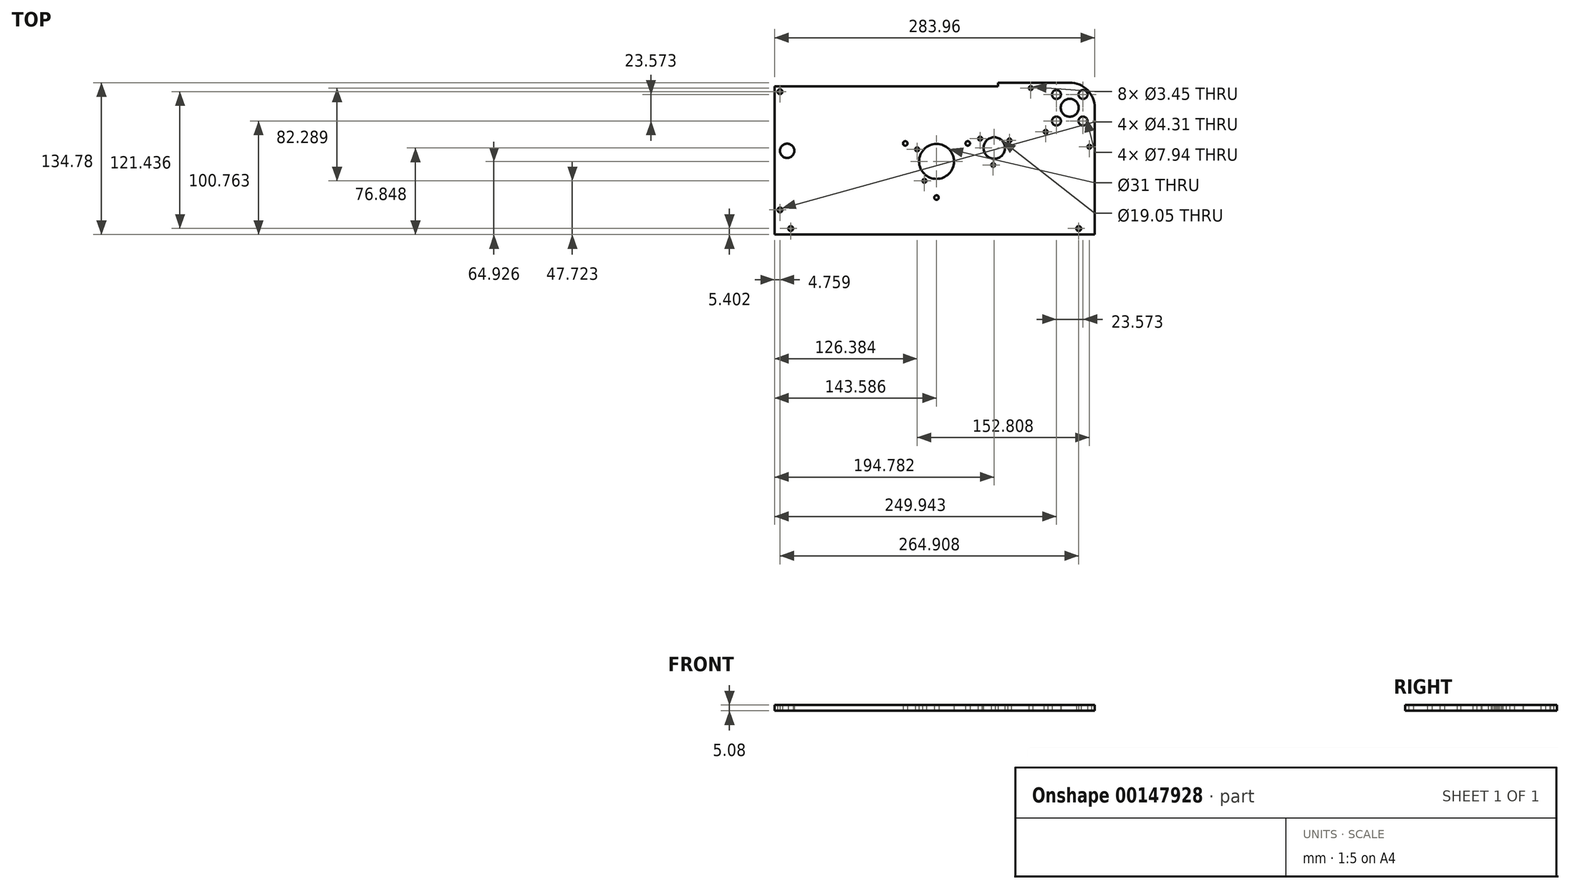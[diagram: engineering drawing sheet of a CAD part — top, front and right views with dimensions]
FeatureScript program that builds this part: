
annotation { "Feature Type Name" : "Feature", "Feature Type Description" : "" }
export const myFeature = defineFeature(function(context is Context, id is Id, definition is map)
    precondition{}
    {
        {
            var Q0;
            Q0=qCreatedBy(makeId("Top.planeOp"),FACE);
            var sketch = newSketch(context, id + "F0", { "sketchPlane" : qUnion([Q0])});
            skCircle(sketch, "E0", {"center": v(0, 0) * mm, "radius": 7.94 * mm});
            skLineSegment(sketch, "E1.bottom", {"start": v(-63.67, 22.23) * mm, "end": v(0, 22.23) * mm});
            skLineSegment(sketch, "E1.top", {"start": v(-261.73, -112.55) * mm, "end": v(22.22, -112.55) * mm});
            skLineSegment(sketch, "E1.left", {"start": v(-261.73, 19.05) * mm, "end": v(-261.73, -112.55) * mm});
            skArc(sketch, "E2", {"start": v(22.23, 0) * mm, "mid": v(15.72, 15.72) * mm, "end": v(0, 22.23) * mm});
            skLineSegment(sketch, "E3", {"start": v(22.23, -112.55) * mm, "end": v(22.23, 0) * mm});
            skLineSegment(sketch, "E4", {"start": v(22.22, -107.15) * mm, "end": v(7.94, -107.15) * mm, "construction": true});
            skCircle(sketch, "E5", {"center": v(7.94, -107.15) * mm, "radius": 2.15 * mm});
            skLineSegment(sketch, "E6", {"start": v(-261.73, -107.15) * mm, "end": v(-247.45, -107.15) * mm, "construction": true});
            skCircle(sketch, "E7", {"center": v(-247.45, -107.15) * mm, "radius": 2.15 * mm});
            skLineSegment(sketch, "E8", {"start": v(-256.97, 19.05) * mm, "end": v(-256.97, 14.29) * mm, "construction": true});
            skLineSegment(sketch, "E9", {"start": v(-256.97, 14.29) * mm, "end": v(-261.73, 14.29) * mm, "construction": true});
            skLineSegment(sketch, "E10", {"start": v(-256.97, 14.29) * mm, "end": v(-256.97, -90.64) * mm, "construction": true});
            skLineSegment(sketch, "E11", {"start": v(-256.97, -90.64) * mm, "end": v(-256.97, -107.15) * mm, "construction": true});
            skCircle(sketch, "E12", {"center": v(-256.97, -90.64) * mm, "radius": 2.15 * mm});
            skCircle(sketch, "E13", {"center": v(-256.97, 14.29) * mm, "radius": 2.15 * mm});
            skCircle(sketch, "E14", {"center": v(-118.14, -47.62) * mm, "radius": 15.5 * mm});
            skCircle(sketch, "E15.cCircle", {"center": v(-118.14, -47.62) * mm, "radius": 16 * mm, "construction": true});
            skLineSegment(sketch, "E15.0", {"start": v(-145.86, -31.62) * mm, "end": v(-90.43, -31.62) * mm, "construction": true});
            skLineSegment(sketch, "E15.1", {"start": v(-90.43, -31.62) * mm, "end": v(-118.14, -79.62) * mm, "construction": true});
            skLineSegment(sketch, "E15.2", {"start": v(-118.14, -79.62) * mm, "end": v(-145.86, -31.62) * mm, "construction": true});
            skPoint(sketch, "E15.0.midPoint", {"position": v(-118.14, -31.62) * mm});
            skLineSegment(sketch, "E16", {"start": v(-118.14, -47.62) * mm, "end": v(-118.14, -79.62) * mm, "construction": true});
            skCircle(sketch, "E17", {"center": v(-145.86, -31.62) * mm, "radius": 2 * mm});
            skCircle(sketch, "E18", {"center": v(-90.43, -31.62) * mm, "radius": 2 * mm});
            skCircle(sketch, "E19", {"center": v(-118.14, -79.62) * mm, "radius": 2 * mm});
            skLineSegment(sketch, "E20", {"start": v(-118.14, -47.62) * mm, "end": v(-66.95, -35.7) * mm, "construction": true});
            skCircle(sketch, "E21", {"center": v(-66.95, -35.7) * mm, "radius": 9.53 * mm});
            skCircle(sketch, "E22", {"center": v(-66.95, -35.7) * mm, "radius": 11.11 * mm, "construction": true});
            skCircle(sketch, "E23", {"center": v(-53.44, -29) * mm, "radius": 3.97 * mm, "construction": true});
            skLineSegment(sketch, "E24", {"start": v(-118.14, -79.62) * mm, "end": v(-118.14, -112.55) * mm, "construction": true});
            skCircle(sketch, "E25", {"center": v(-118.14, -47.62) * mm, "radius": 37.5 * mm, "construction": true});
            skLineSegment(sketch, "E26", {"start": v(-66.95, -35.7) * mm, "end": v(0, 0) * mm, "construction": true});
            skLineSegment(sketch, "E27", {"start": v(-118.14, -47.62) * mm, "end": v(-132.1, -50.87) * mm, "construction": true});
            skLineSegment(sketch, "E28", {"start": v(-135.35, -36.92) * mm, "end": v(-128.85, -64.83) * mm, "construction": true});
            skCircle(sketch, "E29", {"center": v(-135.35, -36.92) * mm, "radius": 4.76 * mm, "construction": true});
            skCircle(sketch, "E30", {"center": v(-135.35, -36.92) * mm, "radius": 1.73 * mm});
            skCircle(sketch, "E31", {"center": v(-128.85, -64.83) * mm, "radius": 1.73 * mm});
            skLineSegment(sketch, "E32", {"start": v(-135.35, -36.92) * mm, "end": v(-118.14, -47.62) * mm, "construction": true});
            skLineSegment(sketch, "E33", {"start": v(0, 0) * mm, "end": v(17.46, -34.55) * mm, "construction": true});
            skLineSegment(sketch, "E34", {"start": v(0, 0) * mm, "end": v(-21.33, -21.33) * mm, "construction": true});
            skLineSegment(sketch, "E35", {"start": v(0, 0) * mm, "end": v(-34.55, 17.46) * mm, "construction": true});
            skCircle(sketch, "E36", {"center": v(-34.55, 17.46) * mm, "radius": 4.76 * mm, "construction": true});
            skCircle(sketch, "E37", {"center": v(-34.55, 17.46) * mm, "radius": 1.73 * mm});
            skCircle(sketch, "E38", {"center": v(-21.33, -21.33) * mm, "radius": 1.73 * mm});
            skCircle(sketch, "E39", {"center": v(17.46, -34.55) * mm, "radius": 1.73 * mm});
            skLineSegment(sketch, "E40", {"start": v(-34.55, 17.46) * mm, "end": v(-21.33, -21.33) * mm, "construction": true});
            skLineSegment(sketch, "E41", {"start": v(17.46, -34.55) * mm, "end": v(-21.33, -21.33) * mm, "construction": true});
            skLineSegment(sketch, "E42", {"start": v(7.94, -107.15) * mm, "end": v(7.94, -112.55) * mm, "construction": true});
            skCircle(sketch, "E43", {"center": v(-90.43, -31.62) * mm, "radius": 6.48 * mm, "construction": true});
            skCircle(sketch, "E44", {"center": v(-66.95, -35.7) * mm, "radius": 17.36 * mm, "construction": true});
            skCircle(sketch, "E45", {"center": v(11.79, 11.79) * mm, "radius": 5.56 * mm, "construction": true});
            skCircle(sketch, "E46", {"center": v(11.79, 11.79) * mm, "radius": 3.97 * mm});
            skCircle(sketch, "E47", {"center": v(11.79, -11.79) * mm, "radius": 3.97 * mm});
            skCircle(sketch, "E48", {"center": v(-11.79, 11.79) * mm, "radius": 3.97 * mm});
            skLineSegment(sketch, "E49.bottom", {"start": v(11.79, 11.79) * mm, "end": v(-11.79, 11.79) * mm, "construction": true});
            skLineSegment(sketch, "E49.top", {"start": v(11.79, -11.79) * mm, "end": v(-11.79, -11.79) * mm, "construction": true});
            skLineSegment(sketch, "E49.left", {"start": v(11.79, 11.79) * mm, "end": v(11.79, -11.79) * mm, "construction": true});
            skLineSegment(sketch, "E49.right", {"start": v(-11.79, 11.79) * mm, "end": v(-11.79, -11.79) * mm, "construction": true});
            skCircle(sketch, "E50", {"center": v(-11.79, -11.79) * mm, "radius": 3.97 * mm});
            skCircle(sketch, "E51.cCircle", {"center": v(-66.95, -35.7) * mm, "radius": 7.54 * mm, "construction": true});
            skLineSegment(sketch, "E51.0", {"start": v(-67.9, -50.75) * mm, "end": v(-79.5, -27.35) * mm, "construction": true});
            skLineSegment(sketch, "E51.1", {"start": v(-79.5, -27.35) * mm, "end": v(-53.44, -29) * mm, "construction": true});
            skLineSegment(sketch, "E51.2", {"start": v(-53.44, -29) * mm, "end": v(-67.9, -50.75) * mm, "construction": true});
            skCircle(sketch, "E52", {"center": v(-79.5, -27.35) * mm, "radius": 1.73 * mm});
            skCircle(sketch, "E53", {"center": v(-67.9, -50.75) * mm, "radius": 1.73 * mm});
            skCircle(sketch, "E54", {"center": v(-53.44, -29) * mm, "radius": 1.73 * mm});
            skCircle(sketch, "E55", {"center": v(-90.43, -31.62) * mm, "radius": 6.17 * mm, "construction": true});
            skCircle(sketch, "E56", {"center": v(-79.5, -27.35) * mm, "radius": 5.56 * mm, "construction": true});
            skLineSegment(sketch, "E57.top", {"start": v(-63.67, 19.05) * mm, "end": v(-261.73, 19.05) * mm});
            skLineSegment(sketch, "E57.left", {"start": v(-63.67, 22.23) * mm, "end": v(-63.67, 19.05) * mm});
            skCircle(sketch, "E58", {"center": v(0, 0) * mm, "radius": 63.67 * mm, "construction": true});
            skLineSegment(sketch, "E59", {"start": v(-63.67, 19.05) * mm, "end": v(-63.67, -8.33) * mm, "construction": true});
            skLineSegment(sketch, "E60", {"start": v(-66.95, -8.33) * mm, "end": v(-63.67, -8.33) * mm, "construction": true});
            skLineSegment(sketch, "E61", {"start": v(-66.95, -8.33) * mm, "end": v(-66.95, -35.7) * mm, "construction": true});
            skLineSegment(sketch, "E62", {"start": v(-256.97, -38.18) * mm, "end": v(-250.62, -38.18) * mm, "construction": true});
            skCircle(sketch, "E63", {"center": v(-250.62, -38.18) * mm, "radius": 6.35 * mm});
            skSolve(sketch);
        }
        {
            var Q0;
            Q0=qSketchRegion(id+"F0",true);
            extrude(context, id + "F1", {"entities" : qUnion([Q0]), "depth" : 5.08 * mm});
        }
    });
